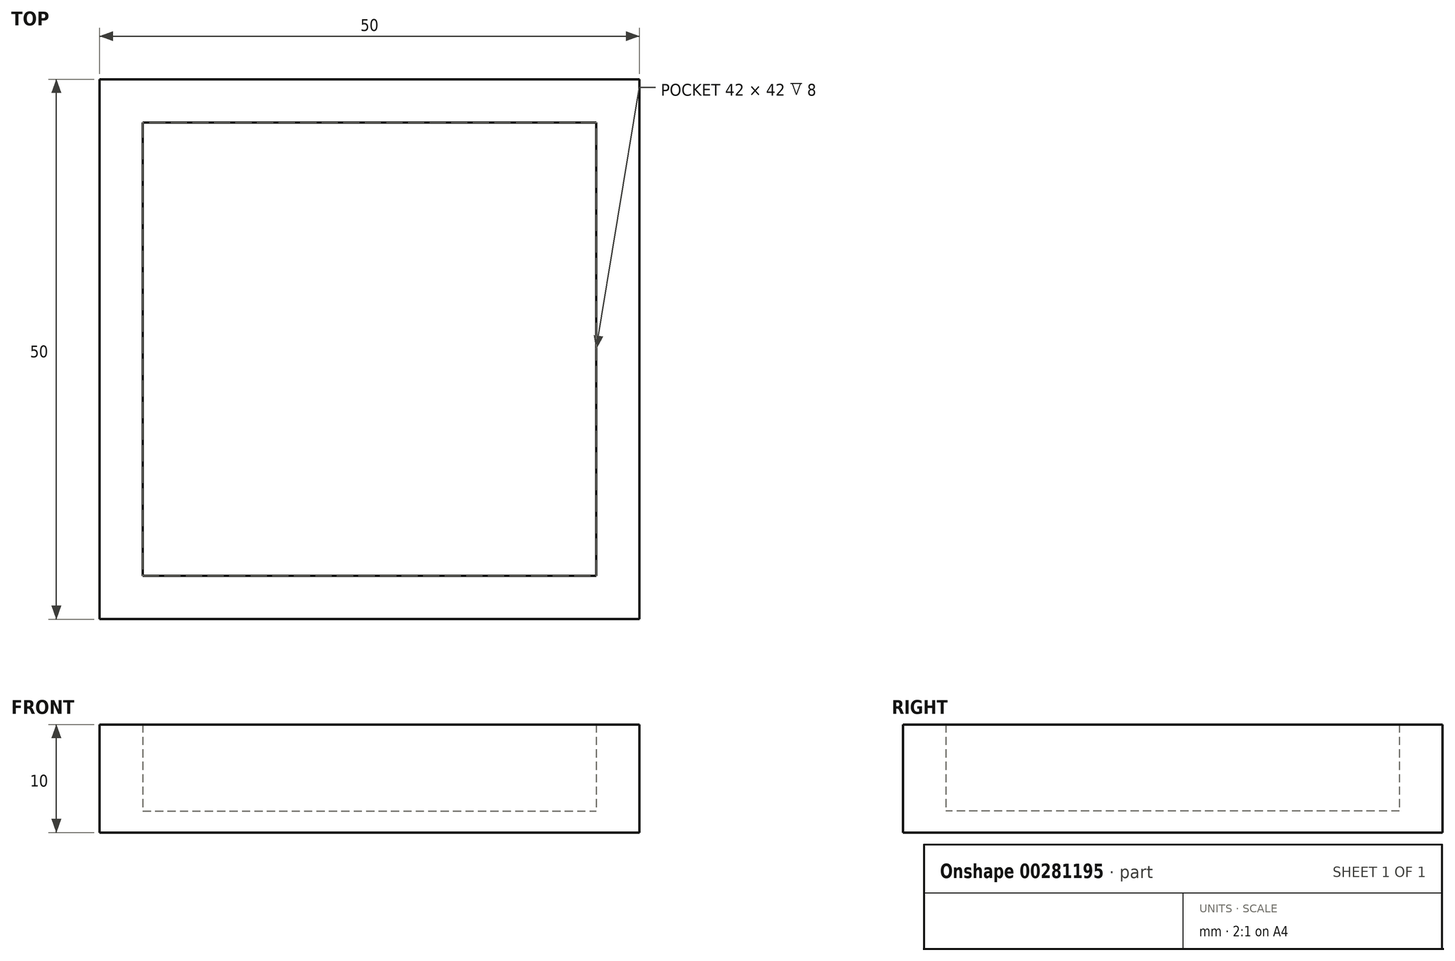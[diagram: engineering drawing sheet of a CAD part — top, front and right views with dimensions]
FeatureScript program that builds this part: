
annotation { "Feature Type Name" : "Feature", "Feature Type Description" : "" }
export const myFeature = defineFeature(function(context is Context, id is Id, definition is map)
    precondition{}
    {
        {
            var Q0;
            Q0=qCreatedBy(makeId("Top.planeOp"),FACE);
            var sketch = newSketch(context, id + "F0", { "sketchPlane" : qUnion([Q0])});
            skLineSegment(sketch, "E0.bottom", {"start": v(-25.66, 19.35) * mm, "end": v(24.34, 19.35) * mm});
            skLineSegment(sketch, "E0.top", {"start": v(-25.66, -30.65) * mm, "end": v(24.34, -30.65) * mm});
            skLineSegment(sketch, "E0.left", {"start": v(-25.66, 19.35) * mm, "end": v(-25.66, -30.65) * mm});
            skLineSegment(sketch, "E0.right", {"start": v(24.34, 19.35) * mm, "end": v(24.34, -30.65) * mm});
            skLineSegment(sketch, "E1.0", {"start": v(-21.66, 15.35) * mm, "end": v(20.34, 15.35) * mm});
            skLineSegment(sketch, "E1.1", {"start": v(-21.66, 15.35) * mm, "end": v(-21.66, -26.65) * mm});
            skLineSegment(sketch, "E1.2", {"start": v(-21.66, -26.65) * mm, "end": v(20.34, -26.65) * mm});
            skLineSegment(sketch, "E1.3", {"start": v(20.34, 15.35) * mm, "end": v(20.34, -26.65) * mm});
            skSolve(sketch);
        }
        {
            var Q0;
            Q0=makeQuery(id+"F0.imprint","IMPRINT",FACE,{"disambiguationData":[TD([[makeQuery(id+"F0.imprint","IMPRINT",EDGE,{"derivedFrom":sQuery(id+"F0.wireOp",EDGE,"E0.bottom")}),-1.0]])]});
            extrude(context, id + "F1", {"entities" : qUnion([Q0]), "depth" : 8 * mm});
        }
        {
            var Q0;
            Q0=makeQuery(id+"F1.opExtrude","CAP_FACE",FACE,{"disambiguationData":[OSD([sQuery(id+"F0.wireOp",EDGE,"E0.bottom"),sQuery(id+"F0.wireOp",EDGE,"E0.top"),sQuery(id+"F0.wireOp",EDGE,"E0.left"),sQuery(id+"F0.wireOp",EDGE,"E0.right"),sQuery(id+"F0.wireOp",EDGE,"E1.0"),sQuery(id+"F0.wireOp",EDGE,"E1.1"),sQuery(id+"F0.wireOp",EDGE,"E1.2"),sQuery(id+"F0.wireOp",EDGE,"E1.3")])],"isStart":true});
            var sketch = newSketch(context, id + "F2", { "sketchPlane" : qUnion([Q0])});
            skLineSegment(sketch, "E2.bottom", {"start": v(-25.66, 30.65) * mm, "end": v(24.34, 30.65) * mm});
            skLineSegment(sketch, "E2.top", {"start": v(-25.66, -19.35) * mm, "end": v(24.34, -19.35) * mm});
            skLineSegment(sketch, "E2.left", {"start": v(-25.66, 30.65) * mm, "end": v(-25.66, -19.35) * mm});
            skLineSegment(sketch, "E2.right", {"start": v(24.34, 30.65) * mm, "end": v(24.34, -19.35) * mm});
            skSolve(sketch);
        }
        {
            var Q0;
            Q0 = qSketchRegion(id + "F2", true);
            extrude(context, id + "F3", {"entities" : qUnion([Q0]), "operationType" : NewBodyOperationType.ADD, "depth" : 2 * mm});
        }
    });
